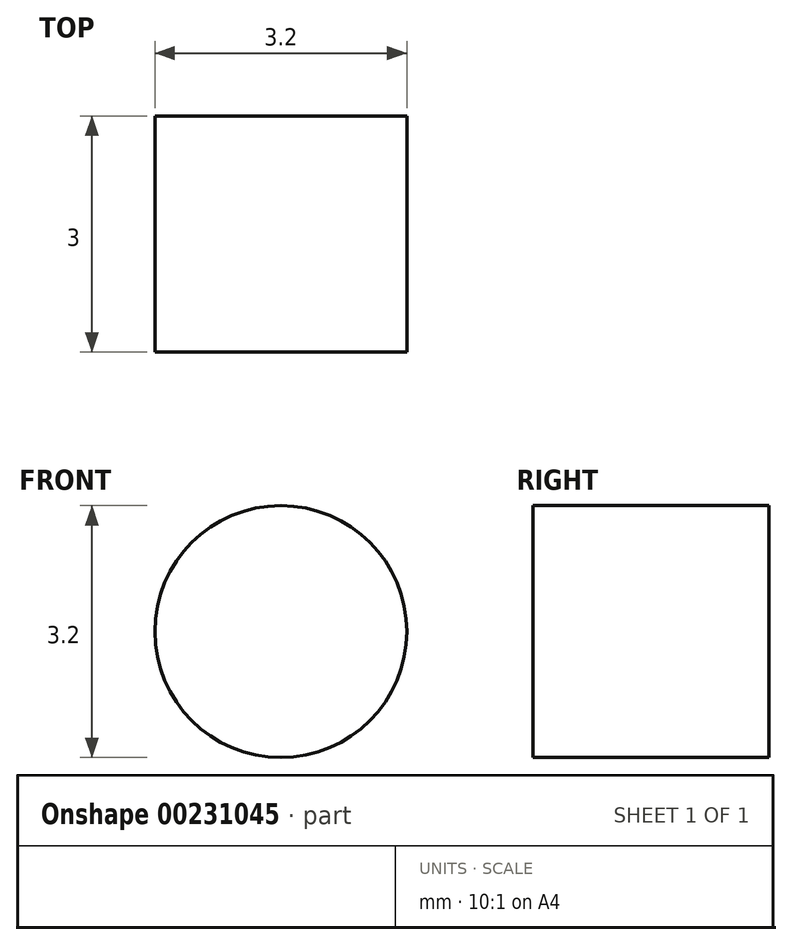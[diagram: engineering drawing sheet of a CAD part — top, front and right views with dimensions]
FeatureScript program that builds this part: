
annotation { "Feature Type Name" : "Feature", "Feature Type Description" : "" }
export const myFeature = defineFeature(function(context is Context, id is Id, definition is map)
    precondition{}
    {
        {
            var Q0;
            Q0=qCreatedBy(makeId("Top.planeOp"),FACE);
            var sketch = newSketch(context, id + "F0", { "sketchPlane" : qUnion([Q0])});
            skCircle(sketch, "E0", {"center": v(0, 0) * mm, "radius": 15 * mm});
            skCircle(sketch, "E1", {"center": v(0, 0) * mm, "radius": 17 * mm});
            skLineSegment(sketch, "E2.bottom", {"start": v(-17, 0) * mm, "end": v(17, 0) * mm});
            skLineSegment(sketch, "E2.top", {"start": v(-17, 32) * mm, "end": v(17, 32) * mm});
            skLineSegment(sketch, "E2.left", {"start": v(-17, 0) * mm, "end": v(-17, 29) * mm});
            skLineSegment(sketch, "E2.right", {"start": v(17, 0) * mm, "end": v(17, 29) * mm});
            skLineSegment(sketch, "E3.bottom", {"start": v(-27, 32) * mm, "end": v(27, 32) * mm});
            skLineSegment(sketch, "E3.top", {"start": v(-27, 29) * mm, "end": v(-17, 29) * mm});
            skLineSegment(sketch, "E3.left", {"start": v(-27, 32) * mm, "end": v(-27, 29) * mm});
            skLineSegment(sketch, "E3.right", {"start": v(27, 32) * mm, "end": v(27, 29) * mm});
            skLineSegment(sketch, "E4.bottom", {"start": v(13.64, 29) * mm, "end": v(-13.64, 29) * mm});
            skLineSegment(sketch, "E4.top", {"start": v(13.64, 17.93) * mm, "end": v(-13.64, 17.93) * mm});
            skLineSegment(sketch, "E4.left", {"start": v(13.64, 29) * mm, "end": v(13.64, 17.93) * mm});
            skLineSegment(sketch, "E4.right", {"start": v(-13.64, 29) * mm, "end": v(-13.64, 17.93) * mm});
            skPoint(sketch, "E4.middle", {"position": v(0, 23.47) * mm});
            skLineSegment(sketch, "E5.trimOffspring", {"start": v(-13.64, 29) * mm, "end": v(13.64, 29) * mm});
            skLineSegment(sketch, "E6.trimOffspring", {"start": v(17, 29) * mm, "end": v(27, 29) * mm});
            skSolve(sketch);
        }
        {
            var Q0;
            {var subQ3=sQuery(id+"F0.wireOp",EDGE,"E2.left");Q0=makeQuery(id+"F0.imprint","IMPRINT",FACE,{"disambiguationData":[TD([[makeQuery(id+"F0.imprint","IMPRINT",EDGE,{"derivedFrom":subQ3}),-1.0]])]});}
            var Q1;
            {var subQ0=sQuery(id+"F0.wireOp",EDGE,"E2.bottom");var subQ1=sQuery(id+"F0.wireOp",EDGE,"E0");var subQ2=makeQuery(id+"F0.imprint","INTERSECT",VERTEX,{"disambiguationData":[OD(0.0)],"derivedFrom":[subQ1,subQ0]});Q1=makeQuery(id+"F0.imprint","IMPRINT",FACE,{"disambiguationData":[TD([[makeQuery(id+"F0.imprint","IMPRINT",EDGE,{"disambiguationData":[TD([[subQ2,1.0]])],"derivedFrom":subQ1}),-1.0]])]});}
            var Q2;
            {var subQ0=sQuery(id+"F0.wireOp",EDGE,"E2.bottom");var subQ1=sQuery(id+"F0.wireOp",EDGE,"E0");var subQ2=makeQuery(id+"F0.imprint","INTERSECT",VERTEX,{"disambiguationData":[OD(0.0)],"derivedFrom":[subQ1,subQ0]});Q2=makeQuery(id+"F0.imprint","IMPRINT",FACE,{"disambiguationData":[TD([[makeQuery(id+"F0.imprint","IMPRINT",EDGE,{"disambiguationData":[TD([[subQ2,-1.0]])],"derivedFrom":subQ1}),-1.0]])]});}
            extrude(context, id + "F1", {"entities" : qUnion([Q0, Q1, Q2]), "depth" : 10 * mm});
        }
        {
            var Q0;
            Q0=makeQuery(id+"F1.opExtrude","SWEPT_FACE",FACE,{"disambiguationData":[OSD([sQuery(id+"F0.wireOp",EDGE,"E3.bottom")])]});
            var sketch = newSketch(context, id + "F2", { "sketchPlane" : qUnion([Q0])});
            skLineSegment(sketch, "E7", {"start": v(-27, 5) * mm, "end": v(27, 5) * mm});
            skCircle(sketch, "E8", {"center": v(-24.5, 5) * mm, "radius": 1.6 * mm});
            skCircle(sketch, "E9", {"center": v(24.5, 5) * mm, "radius": 1.6 * mm});
            skSolve(sketch);
        }
        {
            var Q0;
            {var subQ0=sQuery(id+"F2.wireOp",EDGE,"E8");var subQ1=sQuery(id+"F2.wireOp",EDGE,"E7");var subQ2=makeQuery(id+"F2.imprint","INTERSECT",VERTEX,{"disambiguationData":[OD(0.0)],"derivedFrom":[subQ1,subQ0]});Q0=makeQuery(id+"F2.imprint","IMPRINT",FACE,{"disambiguationData":[TD([[makeQuery(id+"F2.imprint","IMPRINT",EDGE,{"disambiguationData":[TD([[subQ2,-1.0]])],"derivedFrom":subQ1}),1.0]])]});}
            var Q1;
            {var subQ0=sQuery(id+"F2.wireOp",EDGE,"E8");var subQ1=sQuery(id+"F2.wireOp",EDGE,"E7");var subQ2=makeQuery(id+"F2.imprint","INTERSECT",VERTEX,{"disambiguationData":[OD(0.0)],"derivedFrom":[subQ1,subQ0]});Q1=makeQuery(id+"F2.imprint","IMPRINT",FACE,{"disambiguationData":[TD([[makeQuery(id+"F2.imprint","IMPRINT",EDGE,{"disambiguationData":[TD([[subQ2,-1.0]])],"derivedFrom":subQ1}),-1.0]])]});}
            var Q2;
            {var subQ0=sQuery(id+"F2.wireOp",EDGE,"E9");var subQ1=sQuery(id+"F2.wireOp",EDGE,"E7");var subQ2=makeQuery(id+"F2.imprint","INTERSECT",VERTEX,{"disambiguationData":[OD(0.0)],"derivedFrom":[subQ1,subQ0]});Q2=makeQuery(id+"F2.imprint","IMPRINT",FACE,{"disambiguationData":[TD([[makeQuery(id+"F2.imprint","IMPRINT",EDGE,{"disambiguationData":[TD([[subQ2,-1.0]])],"derivedFrom":subQ1}),1.0]])]});}
            var Q3;
            {var subQ0=sQuery(id+"F2.wireOp",EDGE,"E9");var subQ1=sQuery(id+"F2.wireOp",EDGE,"E7");var subQ2=makeQuery(id+"F2.imprint","INTERSECT",VERTEX,{"disambiguationData":[OD(0.0)],"derivedFrom":[subQ1,subQ0]});Q3=makeQuery(id+"F2.imprint","IMPRINT",FACE,{"disambiguationData":[TD([[makeQuery(id+"F2.imprint","IMPRINT",EDGE,{"disambiguationData":[TD([[subQ2,-1.0]])],"derivedFrom":subQ1}),-1.0]])]});}
            extrude(context, id + "F3", {"entities" : qUnion([Q0, Q1, Q2, Q3]), "operationType" : NewBodyOperationType.REMOVE, "endBound" : BoundingType.THROUGH_ALL, "oppositeDirection" : true, "depth" : 25 * mm});
        }
    });
